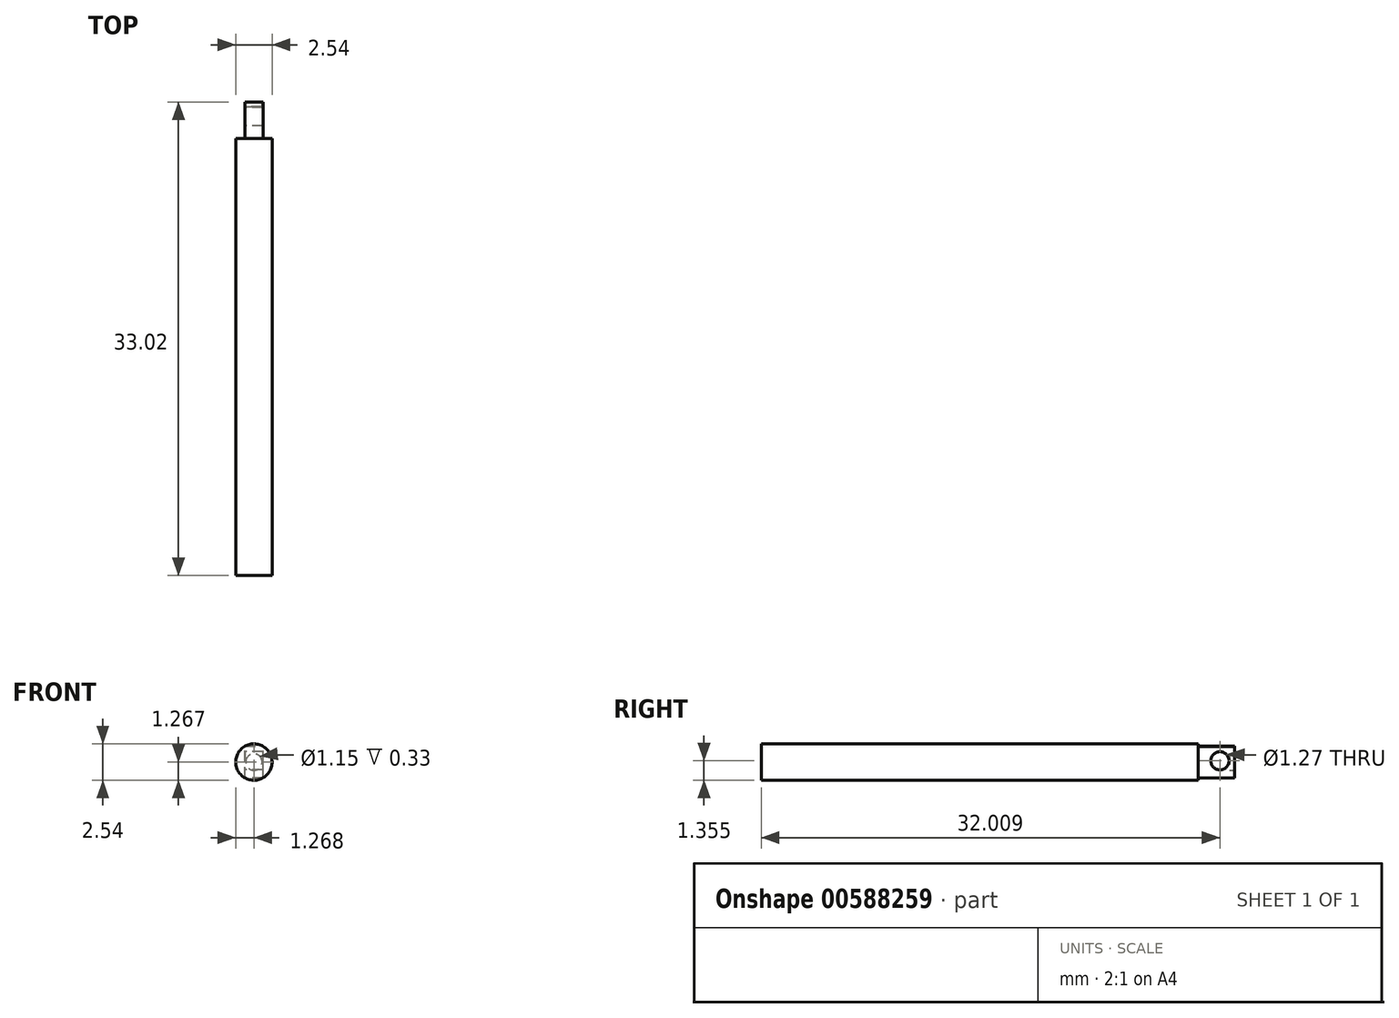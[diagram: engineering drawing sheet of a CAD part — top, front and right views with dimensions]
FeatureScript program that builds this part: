
annotation { "Feature Type Name" : "Feature", "Feature Type Description" : "" }
export const myFeature = defineFeature(function(context is Context, id is Id, definition is map)
    precondition{}
    {
        {
            var Q0;
            Q0=qCreatedBy(makeId("Front.planeOp"),FACE);
            var sketch = newSketch(context, id + "F0", { "sketchPlane" : qUnion([Q0])});
            skCircle(sketch, "E0", {"center": v(-44.91, 42.52) * mm, "radius": 1.27 * mm});
            skSolve(sketch);
        }
        {
            var Q0;
            Q0=makeQuery(id+"F0.imprint","IMPRINT",FACE,{"disambiguationData":[TD([[makeQuery(id+"F0.imprint","IMPRINT",EDGE,{"derivedFrom":sQuery(id+"F0.wireOp",EDGE,"E0")}),1.0]])]});
            extrude(context, id + "F1", {"entities" : qUnion([Q0]), "depth" : 30.48 * mm, "offsetDistance" : 25.4 * mm});
        }
        {
            var Q0;
            Q0=makeQuery(id+"F1.opExtrude","CAP_FACE",FACE,{"disambiguationData":[OSD([sQuery(id+"F0.wireOp",EDGE,"E0")])],"isStart":true});
            var sketch = newSketch(context, id + "F2", { "sketchPlane" : qUnion([Q0])});
            skLineSegment(sketch, "E1", {"start": v(44.28, 42.52) * mm, "end": v(44.28, 43.62) * mm});
            skLineSegment(sketch, "E2", {"start": v(44.28, 43.62) * mm, "end": v(44.28, 41.42) * mm});
            skLineSegment(sketch, "E3", {"start": v(45.55, 41.42) * mm, "end": v(45.55, 43.62) * mm});
            skLineSegment(sketch, "E4", {"start": v(45.55, 43.62) * mm, "end": v(44.28, 43.62) * mm});
            skLineSegment(sketch, "E5", {"start": v(44.28, 41.42) * mm, "end": v(45.55, 41.42) * mm});
            skSolve(sketch);
        }
        {
            var Q0;
            Q0=makeQuery(id+"F2.imprint","IMPRINT",FACE,{"disambiguationData":[TD([[makeQuery(id+"F2.imprint","IMPRINT",EDGE,{"derivedFrom":sQuery(id+"F2.wireOp",EDGE,"E3")}),1.0]])]});
            extrude(context, id + "F3", {"entities" : qUnion([Q0]), "operationType" : NewBodyOperationType.ADD, "depth" : 2.54 * mm, "offsetDistance" : 25.4 * mm});
        }
        {
            var Q0;
            Q0=makeQuery(id+"F3.opExtrude","SWEPT_FACE",FACE,{"disambiguationData":[OSD([sQuery(id+"F2.wireOp",EDGE,"E3")])]});
            var sketch = newSketch(context, id + "F4", { "sketchPlane" : qUnion([Q0])});
            skPoint(sketch, "E6", {"position": v(-1.27, 42.52) * mm});
            skPoint(sketch, "E6.positionSnap0", {"position": v(-2.54, 42.52) * mm});
            skPoint(sketch, "E6.positionSnap1", {"position": v(-1.27, 43.62) * mm});
            skPoint(sketch, "E7", {"position": v(-1.53, 42.52) * mm});
            skPoint(sketch, "E8", {"position": v(-1.53, 42.44) * mm});
            skPoint(sketch, "E9", {"position": v(-1.53, 42.6) * mm});
            skSolve(sketch);
        }
        {
            var Q0;
            Q0=sQuery(id+"F4.wireOp",VERTEX,"E9");
            var Q1;
            Q1=makeQuery(id+"F1.opExtrude","SWEPT_BODY",BODY,{"disambiguationData":[OSD([sQuery(id+"F0.wireOp",EDGE,"E0")])]});
            hole(context, id + "F5", {"style" : HoleStyle.SIMPLE, "endStyle" : HoleEndStyle.THROUGH, "holeDiameter" : 1.27 * mm, "majorDiameter" : 6.35 * mm, "isTappedThrough" : true, "tappedDepth" : 12.7 * mm, "tapClearance" : 3, "locations" : qUnion([Q0]), "scope" : qUnion([Q1])});
        }
        {
            var Q0;
            Q0=makeQuery(id+"F3.opExtrude","CAP_FACE",FACE,{"disambiguationData":[OSD([sQuery(id+"F2.wireOp",EDGE,"E2"),sQuery(id+"F2.wireOp",EDGE,"E3"),sQuery(id+"F2.wireOp",EDGE,"E4"),sQuery(id+"F2.wireOp",EDGE,"E5")])],"isStart":false});
            var sketch = newSketch(context, id + "F6", { "sketchPlane" : qUnion([Q0])});
            skPoint(sketch, "E10.endSnap0", {"position": v(44.91, 43.62) * mm});
            skCircle(sketch, "E11", {"center": v(44.91, 42.52) * mm, "radius": 0.57 * mm});
            skSolve(sketch);
        }
        {
            var Q0;
            Q0=makeQuery(id+"F6.imprint","IMPRINT",FACE,{"disambiguationData":[TD([[makeQuery(id+"F6.imprint","IMPRINT",EDGE,{"derivedFrom":sQuery(id+"F6.wireOp",EDGE,"g1wn0rLb-Ar8s-VLPM-qPLO-g9rIPWuDXMOA")}),1.0]])]});
            var Q1;
            Q1=makeQuery(id+"F6.imprint","IMPRINT",FACE,{"disambiguationData":[TD([[makeQuery(id+"F6.imprint","IMPRINT",EDGE,{"derivedFrom":sQuery(id+"F6.wireOp",EDGE,"E11")}),1.0]])]});
            extrude(context, id + "F7", {"entities" : qUnion([Q0, Q1]), "operationType" : NewBodyOperationType.REMOVE, "oppositeDirection" : true, "depth" : 0.33 * mm, "offsetDistance" : 25.4 * mm});
        }
    });
